# Revit family: Chair-Multi_Purpose-T106-Allermuir-Trillipse Cantilever
name_source: partatom
category: Furniture
revit_build: Autodesk Revit MEP 2012 (Build: 20110309_2315)
units: mm (PartAtom-declared; Revit-internal decimal feet)

## types (1)
- T106
    04 CSI = 12 51 00
    2.5" Casters = No
    95 CSI = 12510
    Advanced Sync Tilt with Multi Position Back = No
    Airflow Back Mesh = Yes
    Assembly Code = E2020200
    Back = Fabric - Allermuir - Upholstery - Pebbled - Smooth - Dark Gray
    Back Rest = Fabric - Allermuir - Upholstery - Pebbled - Smooth - Dark Gray
    Base = Fabric - Allermuir - Upholstery - Pebbled - Chrome - Satin
    Base or Frame = Trilliptical Steel frame in Black EPPC
    Black Components = Yes
    Black GRP Base = No
    Black Gas Lift = No
    Black Plastic Back Membrane = Yes
    Brochure URL = http://www.allermuir.net
    CAD Blocks URL = http://www.allermuir.net
    Color Availability = See price list for material options
    Description = No arms, Plastic back, Upholstered seat, Non-nesting cantilever
    Detachable writing table = Yes
    Fabric Spec Sheets = http://www.allermuir.net
    Height Adjustable Arms = No
    Height Adjustable Arms with Multi funtction Pad = No
    LEED Stats URL = http://www.allermuir.net
    Legs = Fabric - Allermuir - Upholstery - Pebbled - Chrome - Satin
    Lumbar Adjustment = No
    Manufacturer = Allermuir
    Manufacturer Fax = (419) 887 5805
    Model = T106
    Negative Seat Tilt = No
    Optional Feature Notes = Trilliptical Steel frame in Silver EPPC and Polished Chrome,  Plastic back in Light Gray, Dark Gray, Translucent, Orange, Blue, Green & White,
    Overall Depth = 1' - 10 1/16"
    Overall Height = 2' - 9"
    Overall Width = 1' - 8 13/16"
    Pedestal Base = NO
    Plugin Data URL = http://products.ecoscorecard.com
    Polished Aluminum Arm Carrier = No
    Polished Aluminum Base = No
    Pricing URL = http://www.allermuir.net
    Product Line = Trillipse Cantilever
    Product Page URL = http://www.allermuir.net
    Seat = Fabric - Allermuir - Upholstery - Pebbled - Light Brown
    Seat Depth = 1' - 7 11/16"
    Seat Depth Adjustment = No
    Seat Height = 1' - 6"
    Seat Width = 1' - 5"
    Seat or Base = Fabric - Allermuir - Upholstery - Pebbled - Light Brown
    Slimline Upholstery = No
    Specifications URL = http://www.allermuir.net
    Stacks = Yes
    Subcategory = Multi-Purpose Line
    Swaged Tubular Steel Legs = YES
    Two Tone Upholstery = No
    URL = http://www.allermuir.net
    Upholstered Back = NO
    Upholstered Seat = YES
    Weight = 22.0 lb
    ecoScorecard Product Page = http://products.ecoscorecard.com
    ecoScorecard_data = http://thesenatorgroup.ecoscorecard.com

## geometry (parser evidence)
native form markers: Blend x10, Sweep x1
no freeform markers — native parametric forms only
